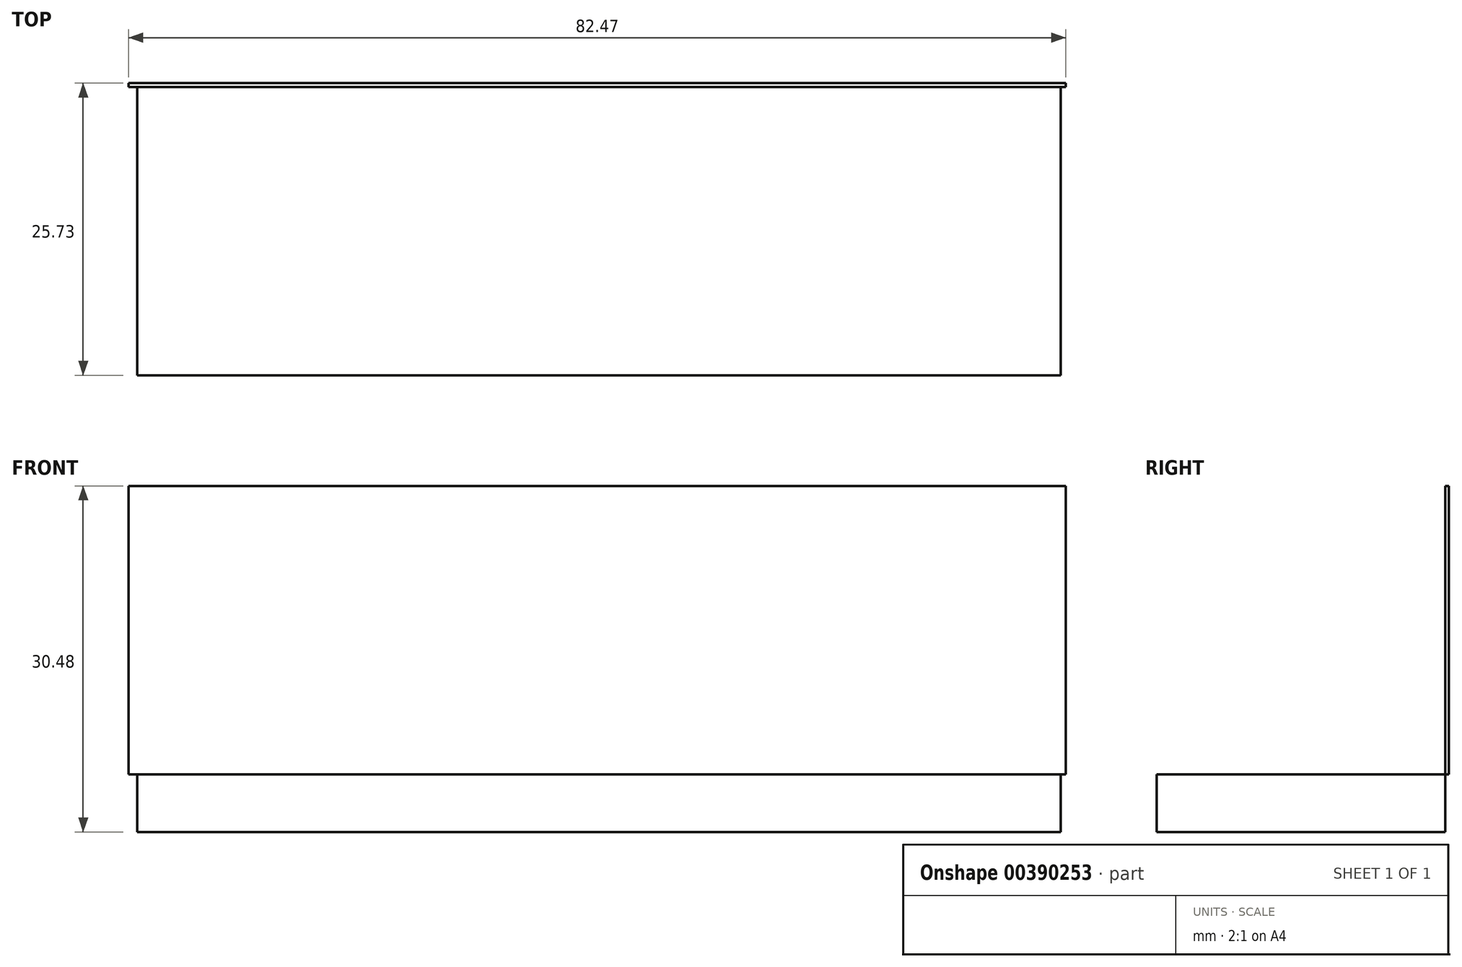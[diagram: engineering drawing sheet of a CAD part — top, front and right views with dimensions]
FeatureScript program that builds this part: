
annotation { "Feature Type Name" : "Feature", "Feature Type Description" : "" }
export const myFeature = defineFeature(function(context is Context, id is Id, definition is map)
    precondition{}
    {
        {
            var Q0;
            Q0=qCreatedBy(makeId("Front.planeOp"),FACE);
            var sketch = newSketch(context, id + "F0", { "sketchPlane" : qUnion([Q0])});
            skLineSegment(sketch, "E0", {"start": v(-38.16, 0) * mm, "end": v(44.31, 0) * mm});
            skLineSegment(sketch, "E1", {"start": v(44.31, 0) * mm, "end": v(44.31, 25.4) * mm});
            skLineSegment(sketch, "E2", {"start": v(44.31, 25.4) * mm, "end": v(-38.16, 25.4) * mm});
            skLineSegment(sketch, "E3", {"start": v(-38.16, 25.4) * mm, "end": v(-38.16, 0) * mm});
            skSolve(sketch);
        }
        {
            var Q0;
            Q0 = qSketchRegion(id + "F0", true);
            extrude(context, id + "F1", {"entities" : qUnion([Q0]), "oppositeDirection" : true, "depth" : 0.33 * mm});
        }
        {
            var Q0;
            Q0=qCreatedBy(makeId("Right.planeOp"),FACE);
            var sketch = newSketch(context, id + "F2", { "sketchPlane" : qUnion([Q0])});
            skLineSegment(sketch, "E4", {"start": v(0, 0) * mm, "end": v(-25.4, 0) * mm});
            skLineSegment(sketch, "E5", {"start": v(-25.4, 0) * mm, "end": v(-25.4, 10.16) * mm});
            skLineSegment(sketch, "E6", {"start": v(-25.4, 10.16) * mm, "end": v(0, 10.16) * mm});
            skSolve(sketch);
        }
        {
            var Q0;
            Q0=sQuery(id+"F2.wireOp",EDGE,"E6");
            var Q1;
            Q1=sQuery(id+"F2.wireOp",EDGE,"E5");
            var Q2;
            Q2=sQuery(id+"F2.wireOp",EDGE,"E4");
            extrude(context, id + "F3", {"bodyType" : ToolBodyType.SURFACE, "surfaceEntities" : qUnion([Q0, Q1, Q2]), "oppositeDirection" : true, "depth" : 0.33 * mm});
        }
        {
            var Q0;
            Q0=qCreatedBy(makeId("Top.planeOp"),FACE);
            var sketch = newSketch(context, id + "F4", { "sketchPlane" : qUnion([Q0])});
            skLineSegment(sketch, "E7", {"start": v(-37.4, 0) * mm, "end": v(-37.4, -25.4) * mm});
            skLineSegment(sketch, "E8", {"start": v(-37.4, -25.4) * mm, "end": v(43.87, -25.4) * mm});
            skLineSegment(sketch, "E9", {"start": v(43.87, -25.4) * mm, "end": v(43.87, 0) * mm});
            skLineSegment(sketch, "E10", {"start": v(43.87, 0) * mm, "end": v(-37.4, 0) * mm});
            skSolve(sketch);
        }
        {
            var Q0;
            Q0 = qSketchRegion(id + "F4", true);
            extrude(context, id + "F5", {"entities" : qUnion([Q0]), "oppositeDirection" : true, "depth" : 5.08 * mm});
        }
    });
